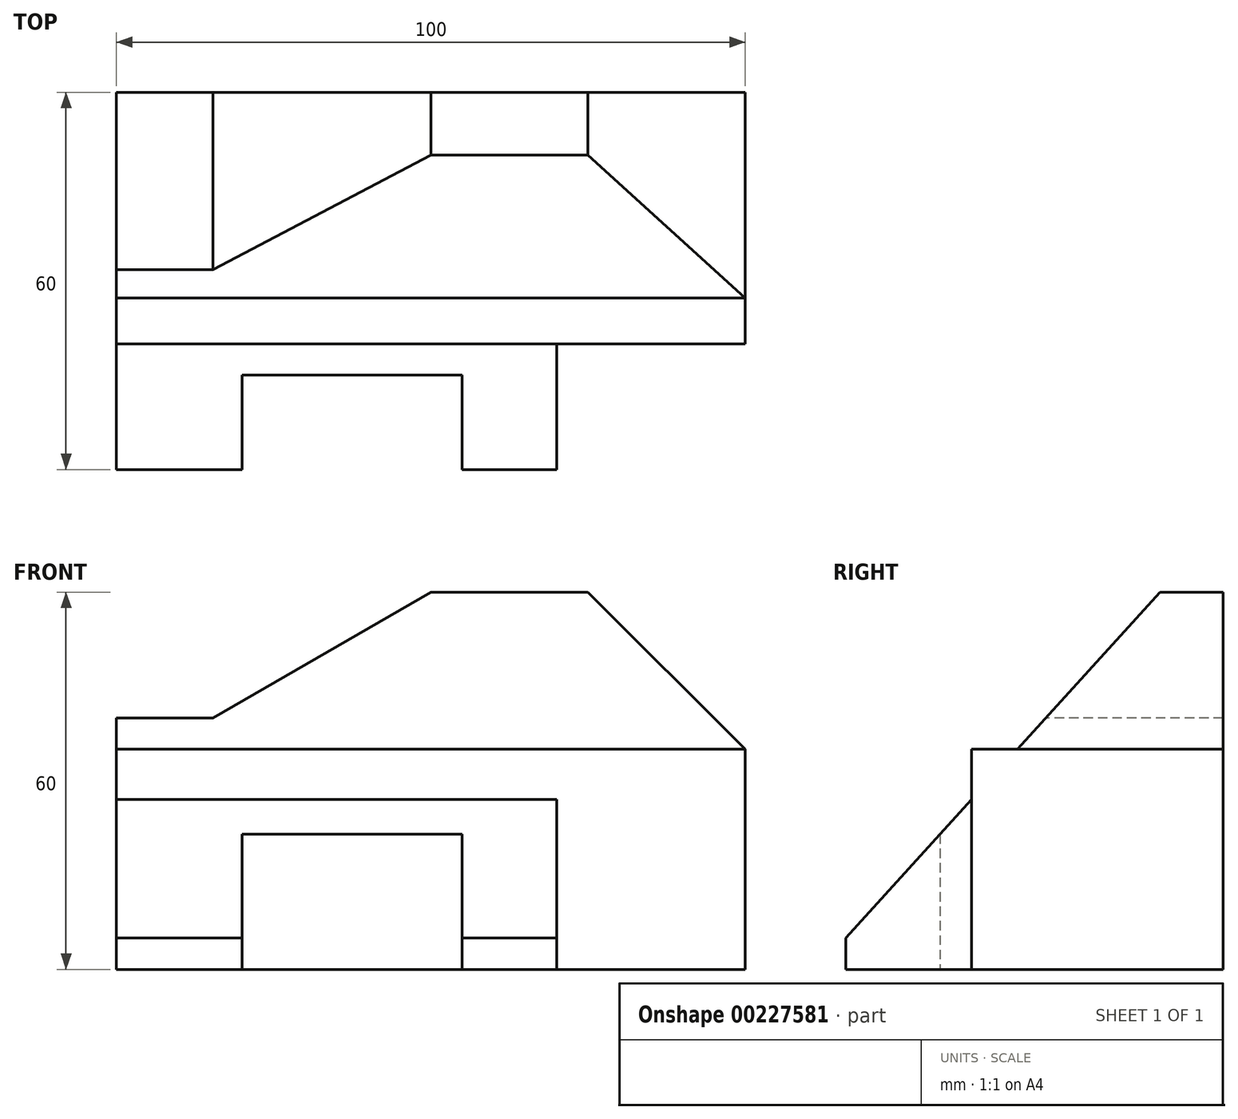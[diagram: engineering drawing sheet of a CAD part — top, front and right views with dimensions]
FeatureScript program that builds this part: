
annotation { "Feature Type Name" : "Feature", "Feature Type Description" : "" }
export const myFeature = defineFeature(function(context is Context, id is Id, definition is map)
    precondition{}
    {
        {
            var Q0;
            Q0=qCreatedBy(makeId("Top.planeOp"),FACE);
            var sketch = newSketch(context, id + "F0", { "sketchPlane" : qUnion([Q0])});
            skLineSegment(sketch, "E0", {"start": v(0, 0) * mm, "end": v(0, 60) * mm});
            skLineSegment(sketch, "E1", {"start": v(0, 60) * mm, "end": v(100, 60) * mm});
            skLineSegment(sketch, "E2", {"start": v(100, 60) * mm, "end": v(100, 20) * mm});
            skLineSegment(sketch, "E3", {"start": v(100, 20) * mm, "end": v(70, 20) * mm});
            skLineSegment(sketch, "E4", {"start": v(70, 20) * mm, "end": v(70, 0) * mm});
            skLineSegment(sketch, "E5", {"start": v(70, 0) * mm, "end": v(55, 0) * mm});
            skLineSegment(sketch, "E6", {"start": v(55, 0) * mm, "end": v(55, 15) * mm});
            skLineSegment(sketch, "E7", {"start": v(55, 15) * mm, "end": v(20, 15) * mm});
            skLineSegment(sketch, "E8", {"start": v(20, 15) * mm, "end": v(20, 0) * mm});
            skLineSegment(sketch, "E9", {"start": v(20, 0) * mm, "end": v(0, 0) * mm});
            skSolve(sketch);
        }
        {
            var Q0;
            Q0 = qSketchRegion(id + "F0", true);
            extrude(context, id + "F1", {"entities" : qUnion([Q0]), "depth" : 60 * mm});
        }
        {
            var Q0;
            Q0=makeQuery(id+"F1.opExtrude","SWEPT_FACE",FACE,{"disambiguationData":[OSD([sQuery(id+"F0.wireOp",EDGE,"E9")])]});
            var sketch = newSketch(context, id + "F2", { "sketchPlane" : qUnion([Q0])});
            skLineSegment(sketch, "E10.0", {"start": v(0, 60) * mm, "end": v(0, 0) * mm, "construction": true});
            skLineSegment(sketch, "E11.0", {"start": v(20, 60) * mm, "end": v(0, 60) * mm, "construction": true});
            skPoint(sketch, "E12.0", {"position": v(37.5, 60) * mm});
            skLineSegment(sketch, "E13.0", {"start": v(55, 60) * mm, "end": v(20, 60) * mm, "construction": true});
            skLineSegment(sketch, "E14.0", {"start": v(70, 60) * mm, "end": v(55, 60) * mm, "construction": true});
            skPoint(sketch, "E15.0", {"position": v(85, 60) * mm});
            skLineSegment(sketch, "E16.0", {"start": v(100, 60) * mm, "end": v(100, 0) * mm, "construction": true});
            skLineSegment(sketch, "E17.0", {"start": v(100, 60) * mm, "end": v(70, 60) * mm, "construction": true});
            skLineSegment(sketch, "E18", {"start": v(0, 40) * mm, "end": v(15.36, 40) * mm});
            skLineSegment(sketch, "E19", {"start": v(15.36, 40) * mm, "end": v(50, 60) * mm});
            skLineSegment(sketch, "E20", {"start": v(75, 60) * mm, "end": v(100, 35) * mm});
            skLineSegment(sketch, "E21", {"start": v(50, 60) * mm, "end": v(0, 60) * mm});
            skLineSegment(sketch, "E22", {"start": v(0, 40) * mm, "end": v(0, 60) * mm});
            skLineSegment(sketch, "E23", {"start": v(75, 60) * mm, "end": v(100, 60) * mm});
            skLineSegment(sketch, "E24", {"start": v(100, 35) * mm, "end": v(100, 60) * mm});
            skSolve(sketch);
        }
        {
            var Q0;
            {var subQ5=sQuery(id+"F2.wireOp",EDGE,"E18");Q0=makeQuery(id+"F2.imprint","IMPRINT",FACE,{"disambiguationData":[TD([[makeQuery(id+"F2.imprint","IMPRINT",EDGE,{"derivedFrom":subQ5}),1.0]])]});}
            var Q1;
            {var subQ0=sQuery(id+"F2.wireOp",EDGE,"E21");var subQ1=sQuery(id+"F2.wireOp",EDGE,"E19");var subQ2=makeQuery(id+"F2.imprint","INTERSECT",VERTEX,{"derivedFrom":[subQ1,subQ0]});Q1=makeQuery(id+"F2.imprint","IMPRINT",FACE,{"disambiguationData":[TD([[makeQuery(id+"F2.imprint","IMPRINT",EDGE,{"disambiguationData":[TD([[subQ2,1.0]])],"derivedFrom":subQ1}),1.0]])]});}
            var Q2;
            Q2=makeQuery(id+"F2.imprint","IMPRINT",FACE,{"disambiguationData":[TD([[makeQuery(id+"F2.imprint","IMPRINT",EDGE,{"derivedFrom":sQuery(id+"F2.wireOp",EDGE,"E20")}),1.0]])]});
            extrude(context, id + "F3", {"entities" : qUnion([Q0, Q1, Q2]), "operationType" : NewBodyOperationType.REMOVE, "endBound" : BoundingType.THROUGH_ALL, "oppositeDirection" : true, "depth" : 25 * mm});
        }
        {
            var Q0;
            Q0=makeQuery(id+"F1.opExtrude","SWEPT_FACE",FACE,{"disambiguationData":[OSD([sQuery(id+"F0.wireOp",EDGE,"E2")])]});
            var sketch = newSketch(context, id + "F4", { "sketchPlane" : qUnion([Q0])});
            skLineSegment(sketch, "E25.0.0", {"start": v(0, 0) * mm, "end": v(20, 0) * mm, "construction": true});
            skLineSegment(sketch, "E25.0.1", {"start": v(20, 0) * mm, "end": v(20, 60) * mm, "construction": true});
            skLineSegment(sketch, "E25.0.2", {"start": v(20, 60) * mm, "end": v(0, 60) * mm, "construction": true});
            skLineSegment(sketch, "E25.0.3", {"start": v(0, 60) * mm, "end": v(0, 0) * mm, "construction": true});
            skLineSegment(sketch, "E26.0.0", {"start": v(20, 60) * mm, "end": v(20, 35) * mm, "construction": true});
            skLineSegment(sketch, "E26.0.1", {"start": v(20, 35) * mm, "end": v(60, 35) * mm, "construction": true});
            skLineSegment(sketch, "E26.0.2", {"start": v(60, 35) * mm, "end": v(60, 60) * mm, "construction": true});
            skLineSegment(sketch, "E26.0.3", {"start": v(60, 60) * mm, "end": v(20, 60) * mm, "construction": true});
            skLineSegment(sketch, "E27.0.0", {"start": v(60, 0) * mm, "end": v(60, 35) * mm, "construction": true});
            skLineSegment(sketch, "E27.0.1", {"start": v(60, 35) * mm, "end": v(20, 35) * mm, "construction": true});
            skLineSegment(sketch, "E27.0.2", {"start": v(20, 35) * mm, "end": v(20, 0) * mm, "construction": true});
            skLineSegment(sketch, "E27.0.3", {"start": v(20, 0) * mm, "end": v(60, 0) * mm, "construction": true});
            skLineSegment(sketch, "E28", {"start": v(50, 60) * mm, "end": v(0, 5) * mm});
            skLineSegment(sketch, "E29", {"start": v(50, 60) * mm, "end": v(0, 60) * mm});
            skLineSegment(sketch, "E30", {"start": v(0, 5) * mm, "end": v(0, 60) * mm});
            skSolve(sketch);
        }
        {
            var Q0;
            {var subQ1=sQuery(id+"F4.wireOp",EDGE,"E29");Q0=makeQuery(id+"F4.imprint","IMPRINT",FACE,{"disambiguationData":[TD([[makeQuery(id+"F4.imprint","IMPRINT",EDGE,{"derivedFrom":subQ1}),1.0]])]});}
            var Q1;
            {var subQ0=sQuery(id+"F4.wireOp",EDGE,"E28");var subQ1=makeQuery(id+"F3.boolean.opBoolean","COPY",EDGE,{"derivedFrom":makeQuery(id+"F3.opExtrude","SWEPT_EDGE",EDGE,{"disambiguationData":[OSD([sQuery(id+"F2.wireOp",EDGE,"E20"),sQuery(id+"F2.wireOp",EDGE,"E24")])]})});var subQ2=makeQuery(id+"F4.imprint","INTERSECT",VERTEX,{"derivedFrom":[subQ1,subQ0]});Q1=makeQuery(id+"F4.imprint","IMPRINT",FACE,{"disambiguationData":[TD([[makeQuery(id+"F4.imprint","IMPRINT",EDGE,{"disambiguationData":[TD([[subQ2,-1.0]])],"derivedFrom":subQ0}),-1.0]])]});}
            extrude(context, id + "F5", {"entities" : qUnion([Q0, Q1]), "operationType" : NewBodyOperationType.REMOVE, "endBound" : BoundingType.THROUGH_ALL, "oppositeDirection" : true, "depth" : 25 * mm});
        }
    });
